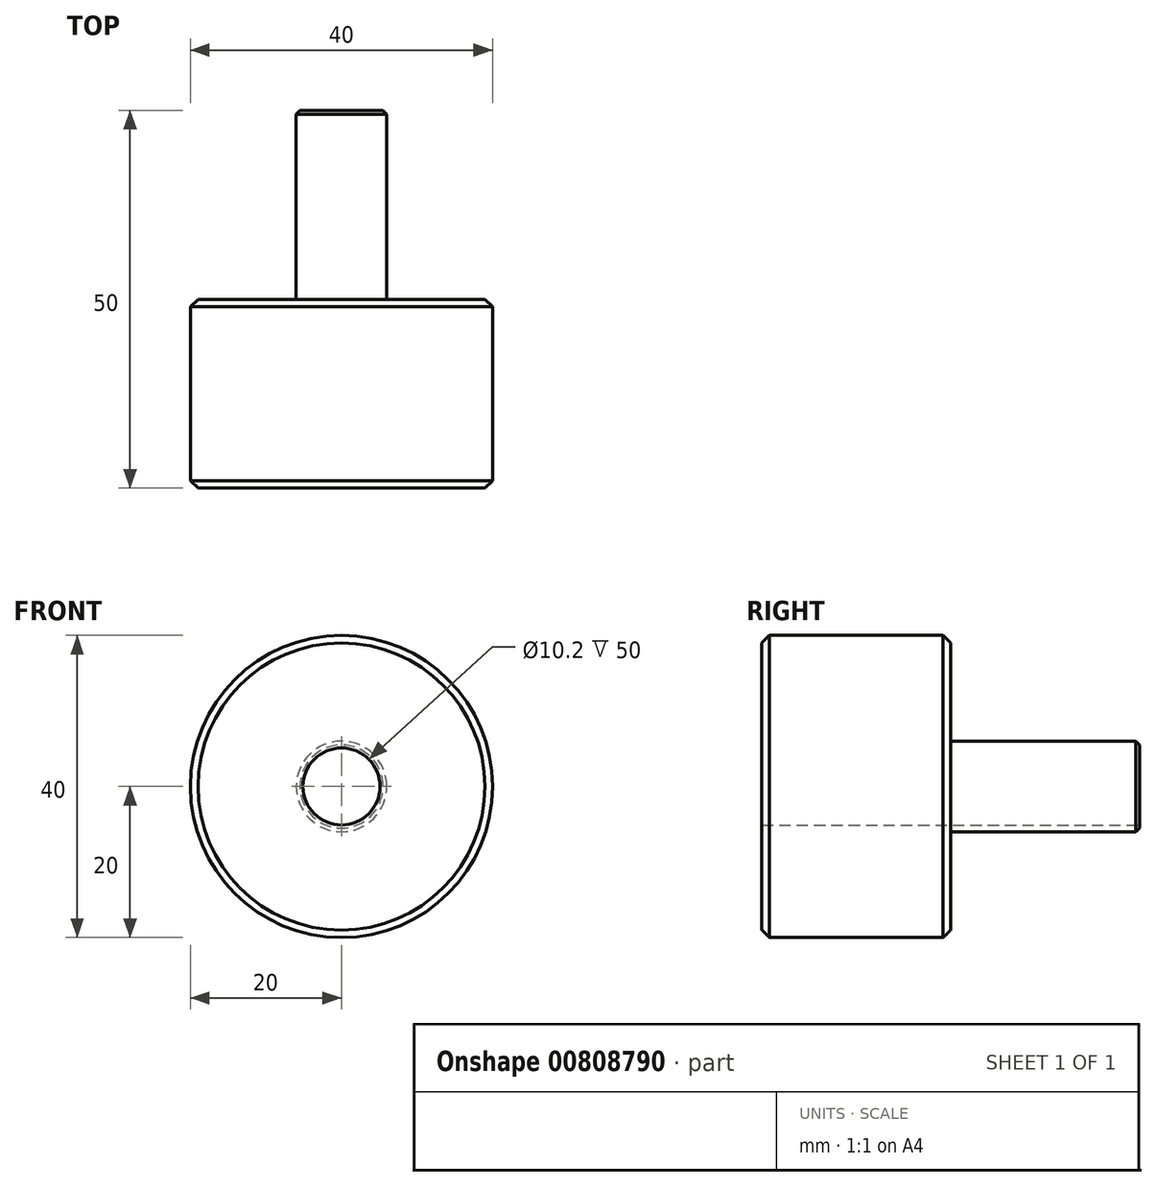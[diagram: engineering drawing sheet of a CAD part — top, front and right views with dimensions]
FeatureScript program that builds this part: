
annotation { "Feature Type Name" : "Feature", "Feature Type Description" : "" }
export const myFeature = defineFeature(function(context is Context, id is Id, definition is map)
    precondition{}
    {
        {
            var Q0;
            Q0=qCreatedBy(makeId("Front.planeOp"),FACE);
            var sketch = newSketch(context, id + "F0", { "sketchPlane" : qUnion([Q0])});
            skCircle(sketch, "E0", {"center": v(0, 0) * mm, "radius": 20 * mm});
            skCircle(sketch, "E1", {"center": v(0, 0) * mm, "radius": 5.1 * mm});
            skSolve(sketch);
        }
        {
            var Q0;
            Q0 = qSketchRegion(id + "F0", true);
            extrude(context, id + "F1", {"entities" : qUnion([Q0]), "depth" : 25 * mm, "offsetDistance" : 25 * mm});
        }
        {
            var Q0;
            Q0=makeQuery(id+"F1.opExtrude","CAP_FACE",FACE,{"disambiguationData":[OSD([sQuery(id+"F0.wireOp",EDGE,"E0")])],"isStart":true});
            var sketch = newSketch(context, id + "F2", { "sketchPlane" : qUnion([Q0])});
            skCircle(sketch, "E2", {"center": v(0, 0) * mm, "radius": 6 * mm});
            skSolve(sketch);
        }
        {
            var Q0;
            Q0=makeQuery(id+"F2.imprint","IMPRINT",FACE,{"disambiguationData":[TD([[makeQuery(id+"F2.imprint","IMPRINT",EDGE,{"derivedFrom":sQuery(id+"F2.wireOp",EDGE,"E2")}),1.0]])]});
            extrude(context, id + "F3", {"entities" : qUnion([Q0]), "operationType" : NewBodyOperationType.ADD, "depth" : 25 * mm, "offsetDistance" : 25 * mm});
        }
        {
            var Q0;
            Q0=makeQuery(id+"F1.opExtrude","CAP_EDGE",EDGE,{"disambiguationData":[OSD([sQuery(id+"F0.wireOp",EDGE,"E0")])],"isStart":false});
            var Q1;
            Q1=makeQuery(id+"F1.opExtrude","CAP_EDGE",EDGE,{"disambiguationData":[OSD([sQuery(id+"F0.wireOp",EDGE,"E0")])],"isStart":true});
            chamfer(context, id + "F4", {"entities" : qUnion([Q0, Q1]), "width" : 1 * mm, "tangentPropagation" : true});
        }
        {
            var Q0;
            Q0=makeQuery(id+"F3.opExtrude","CAP_EDGE",EDGE,{"disambiguationData":[OSD([sQuery(id+"F2.wireOp",EDGE,"E2")])],"isStart":false});
            chamfer(context, id + "F5", {"entities" : qUnion([Q0]), "width" : .5 * mm, "tangentPropagation" : true});
        }
    });
